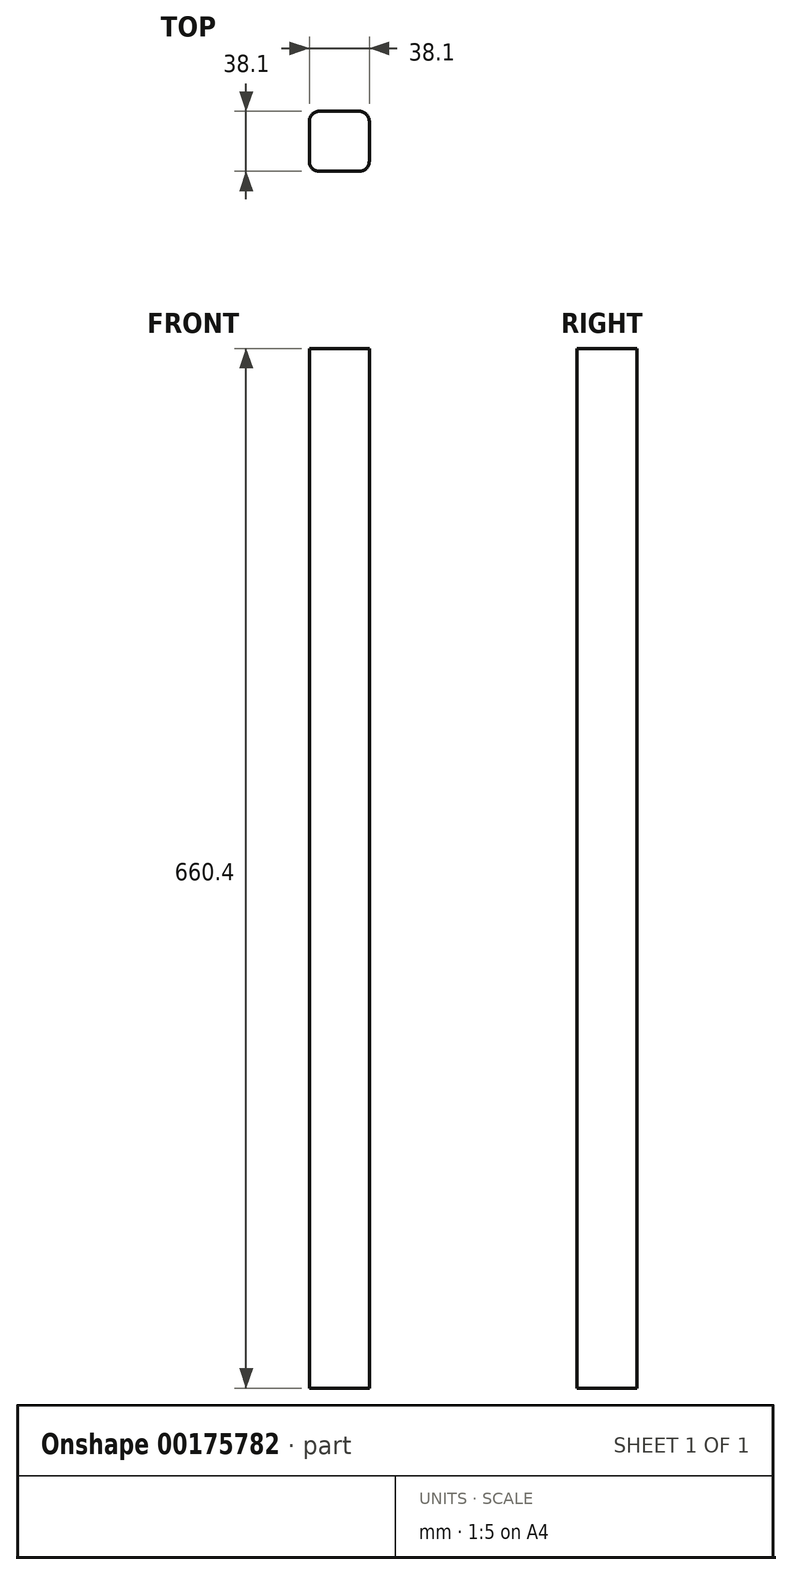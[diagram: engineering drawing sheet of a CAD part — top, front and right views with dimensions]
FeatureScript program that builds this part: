
annotation { "Feature Type Name" : "Feature", "Feature Type Description" : "" }
export const myFeature = defineFeature(function(context is Context, id is Id, definition is map)
    precondition{}
    {
        {
            var Q0;
            Q0=qCreatedBy(makeId("Top.planeOp"),FACE);
            var sketch = newSketch(context, id + "F0", { "sketchPlane" : qUnion([Q0])});
            skLineSegment(sketch, "E0.bottom", {"start": v(12.7, 19.05) * mm, "end": v(-12.7, 19.05) * mm});
            skLineSegment(sketch, "E0.top", {"start": v(12.7, -19.05) * mm, "end": v(-12.7, -19.05) * mm});
            skLineSegment(sketch, "E0.left", {"start": v(19.05, 12.7) * mm, "end": v(19.05, -12.7) * mm});
            skLineSegment(sketch, "E0.right", {"start": v(-19.05, 12.7) * mm, "end": v(-19.05, -12.7) * mm});
            skPoint(sketch, "E0.middle", {"position": v(0, 0) * mm});
            skPoint(sketch, "E1.visualSharp", {"position": v(-19.05, 19.05) * mm});
            skArc(sketch, "E1.filletArc", {"start": v(-12.7, 19.05) * mm, "mid": v(-17.2, 17.2) * mm, "end": v(-19.05, 12.7) * mm});
            skPoint(sketch, "E2.visualSharp", {"position": v(19.05, 19.05) * mm});
            skArc(sketch, "E2.filletArc", {"start": v(19.05, 12.7) * mm, "mid": v(17.2, 17.2) * mm, "end": v(12.7, 19.05) * mm});
            skPoint(sketch, "E3.visualSharp", {"position": v(19.05, -19.05) * mm});
            skArc(sketch, "E3.filletArc", {"start": v(12.7, -19.05) * mm, "mid": v(17.2, -17.2) * mm, "end": v(19.05, -12.7) * mm});
            skPoint(sketch, "E4.visualSharp", {"position": v(-19.05, -19.05) * mm});
            skArc(sketch, "E4.filletArc", {"start": v(-19.05, -12.7) * mm, "mid": v(-17.2, -17.2) * mm, "end": v(-12.7, -19.05) * mm});
            skSolve(sketch);
        }
        {
            var Q0;
            Q0=makeQuery(id+"F0.imprint","IMPRINT",FACE,{"disambiguationData":[TD([[makeQuery(id+"F0.imprint","IMPRINT",EDGE,{"derivedFrom":sQuery(id+"F0.wireOp",EDGE,"E0.bottom")}),1.0]])]});
            extrude(context, id + "F1", {"entities" : qUnion([Q0]), "depth" : 660.4 * mm});
        }
    });
